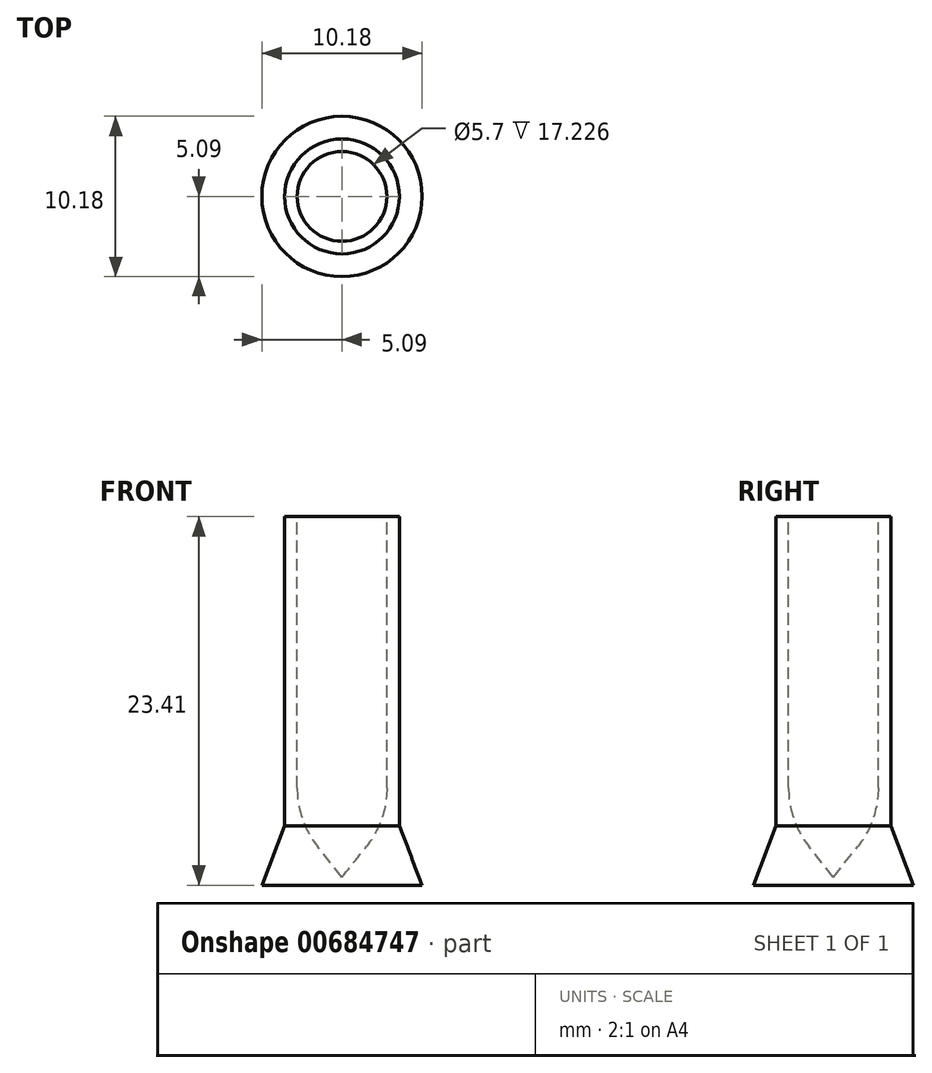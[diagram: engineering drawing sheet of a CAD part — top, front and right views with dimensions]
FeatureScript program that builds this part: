
annotation { "Feature Type Name" : "Feature", "Feature Type Description" : "" }
export const myFeature = defineFeature(function(context is Context, id is Id, definition is map)
    precondition{}
    {
        {
            var Q0;
            Q0=qCreatedBy(makeId("Front.planeOp"),FACE);
            var sketch = newSketch(context, id + "F0", { "sketchPlane" : qUnion([Q0])});
            skLineSegment(sketch, "E0", {"start": v(0, 0) * mm, "end": v(5.1, 0) * mm});
            skLineSegment(sketch, "E1", {"start": v(5.1, 0) * mm, "end": v(5.1, 0) * mm});
            skLineSegment(sketch, "E2", {"start": v(2.85, 23.41) * mm, "end": v(2.85, 6.19) * mm});
            skLineSegment(sketch, "E3", {"start": v(0, 0.5) * mm, "end": v(0, 0) * mm});
            skLineSegment(sketch, "E4", {"start": v(2.85, 23.41) * mm, "end": v(3.65, 23.41) * mm});
            skLineSegment(sketch, "E5", {"start": v(3.65, 23.41) * mm, "end": v(3.65, 3.76) * mm});
            skLineSegment(sketch, "E6", {"start": v(3.65, 3.76) * mm, "end": v(5.1, 0) * mm});
            skLineSegment(sketch, "E7", {"start": v(1.55, 2.47) * mm, "end": v(0, 0.5) * mm});
            skPoint(sketch, "E8.visualSharp", {"position": v(2.85, 4.1) * mm});
            skArc(sketch, "E8.filletArc", {"start": v(1.55, 2.47) * mm, "mid": v(2.52, 4.22) * mm, "end": v(2.85, 6.19) * mm});
            skLineSegment(sketch, "E9", {"start": v(2.85, 24.06) * mm, "end": v(0, 24.06) * mm});
            skLineSegment(sketch, "E10", {"start": v(4.73, 23.41) * mm, "end": v(5.1, 0) * mm});
            skSolve(sketch);
        }
        {
            var Q0;
            Q0=qSketchRegion(id+"F0",true);
            var Q1;
            Q1=sQuery(id+"F0.wireOp",EDGE,"E3");
            revolve(context, id + "F1", {"entities" : qUnion([Q0]), "axis" : qUnion([Q1]), "revolveType" : RevolveType.FULL});
        }
    });
